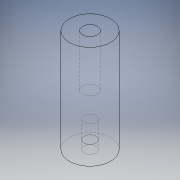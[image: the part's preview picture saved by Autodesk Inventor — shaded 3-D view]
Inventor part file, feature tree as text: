
AUTODESK INVENTOR PART (.ipt)
format: ipt  version: 2019 (Build 230136000, 136)  size: 118,272 bytes
history: native  units: mm
features: sketch x4, extrude x3, hole x1, projected_geometry x1
ambient origin geometry x8: Origin, YZ Plane, XZ Plane, XY Plane, X Axis, Y Axis, Z Axis, Center Point
bodies: Solid1 (feature_tree)
feature tree (9):
  extrude  "Extrusion1"  Depth=15.0mm TaperAngle=0.0deg
  hole  "Hole1"  [1 undecoded]
  extrude  "Extrusion2"  Depth=3.85mm
  extrude  "Extrusion3"  [1 undecoded]
  sketch  "Sketch1"  dims[d0=6.0mm d1=15.0mm d2=0.0mm]
  sketch  "Sketch2"  dims[d3=2.156mm d4=5.69mm d5=11.113mm d6=3.25mm d7=90.0deg d8=7.5mm d9=20.594885mm d10=1.7mm]
  sketch  "Sketch3"  dims[d11=3.85mm d12=0.0mm d13=1.75mm]
  sketch  "Sketch4"  dims[d14=1.25mm d15=0.0mm]
  projected_geometry  "Projected Loop1"
note: 2 required parameter values undecoded (feature->parameter linkage not recoverable at this tier; creation-order binding heuristic only, values carry confidence <= 0.55)
